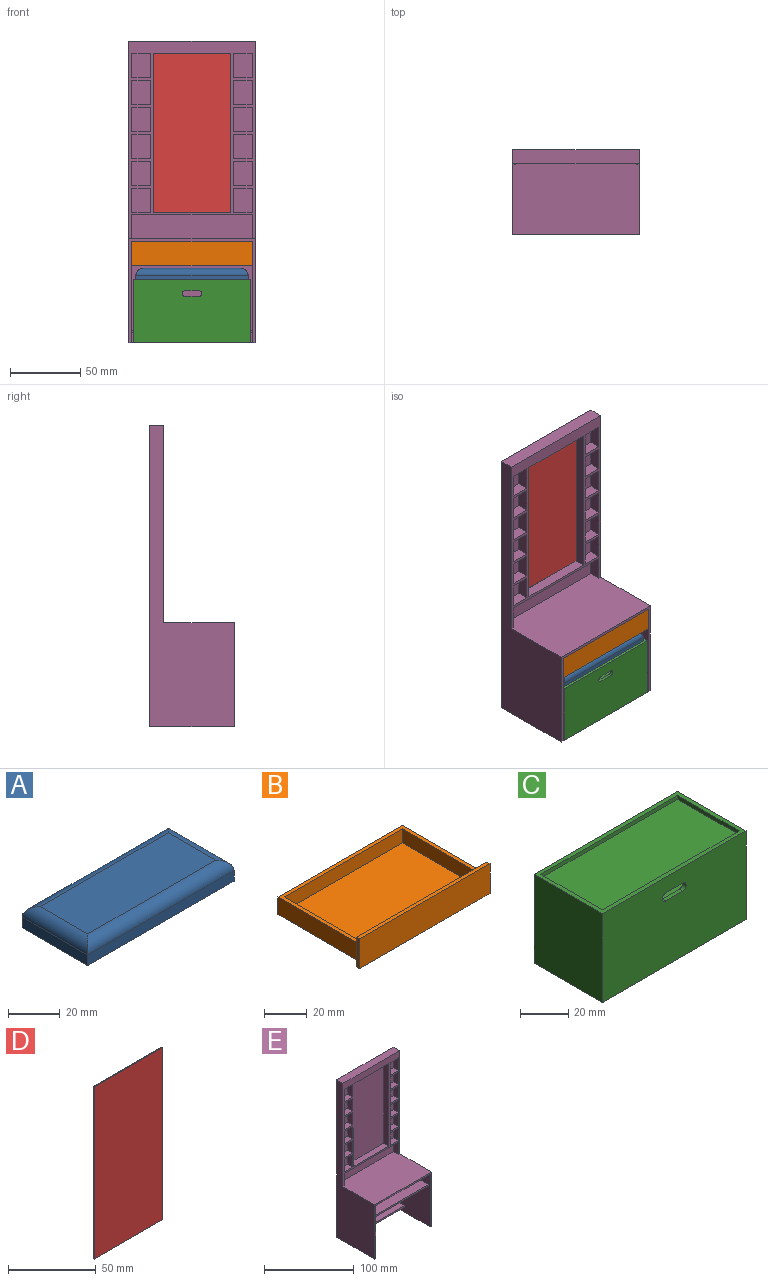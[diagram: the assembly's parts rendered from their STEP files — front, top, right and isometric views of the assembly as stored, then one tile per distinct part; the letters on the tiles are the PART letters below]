
ASSEMBLY  parts=5 mates=4
PART A: 10 faces, bbox 80x36x10 mm
  f0: plane 36x5mm, normal (1,0,0), area 180mm2, adj f1,f3,f5,f6
  f1: plane 80x5mm, normal (0,1,0), area 400mm2, adj f0,f2,f5,f7
  f2: plane 36x5mm, normal (-1,0,0), area 180mm2, adj f1,f3,f5,f9
  f3: plane 80x5mm, normal (0,-1,0), area 400mm2, adj f0,f2,f5,f8
  f4: plane 70x26mm, normal (0,0,1), area 1820mm2, adj f6,f7,f8,f9
  f5: plane 80x36mm, normal (0,0,-1), area 2880mm2, adj f0,f1,f2,f3
  f6: cylinder r=5mm len=36mm, axis (0,-1,0), area 254.2mm2, adj f0,f4,f7,f8
  f7: cylinder r=5mm len=80mm, axis (1,0,0), area 599.8mm2, adj f1,f4,f6,f9
  f8: cylinder r=5mm len=80mm, axis (-1,0,0), area 599.8mm2, adj f3,f4,f6,f9
  f9: cylinder r=5mm len=36mm, axis (0,1,0), area 254.2mm2, adj f2,f4,f7,f8
PART B: 15 faces, bbox 86x56x17 mm
  f0: plane 17x2mm, normal (1,0,0), area 34mm2, adj f5,f6,f7,f8
  f1: plane 82x10mm, normal (0,1,0), area 820mm2, adj f3,f4,f13,f14
  f2: plane 17x2mm, normal (-1,0,0), area 34mm2, adj f5,f6,f7,f8
  f3: plane 82x54mm, normal (0,0,-1), area 4428mm2, adj f1,f8,f13,f14
  f4: plane 82x54mm, normal (0,0,1), area 372mm2, adj f1,f8,f9,f10,f11,f13,f14
  f5: plane 86x2mm, normal (0,0,-1), area 172mm2, adj f0,f2,f7,f8
  f6: plane 86x2mm, normal (0,0,1), area 172mm2, adj f0,f2,f7,f8
  f7: plane 86x17mm, normal (0,-1,0), area 1462mm2, adj f0,f2,f5,f6
  f8: plane 86x17mm, normal (0,1,0), area 1266mm2, adj f0,f2,f3,f4,f5,f6,f10,f11
  f9: plane 78x8mm, normal (0,-1,0), area 624mm2, adj f4,f10,f11,f12
  f10: plane 52x8mm, normal (1,0,0), area 416mm2, adj f4,f8,f9,f12
  f11: plane 52x8mm, normal (-1,0,0), area 416mm2, adj f4,f8,f9,f12
  f12: plane 78x52mm, normal (0,0,1), area 4056mm2, adj f8,f9,f10,f11
  f13: plane 54x10mm, normal (-1,0,0), area 540mm2, adj f1,f3,f4,f8
  f14: plane 54x10mm, normal (1,0,0), area 540mm2, adj f1,f3,f4,f8
PART C: 25 faces, bbox 84x40x45 mm
  f0: plane 84x45mm, normal (0,1,0), area 820mm2, adj f1,f2,f3,f4,f6,f7,f8,f9
  f1: plane 45x40mm, normal (-1,0,0), area 1800mm2, adj f0,f2,f4,f5
  f2: plane 84x40mm, normal (0,0,-1), area 3360mm2, adj f0,f1,f3,f5
  f3: plane 45x40mm, normal (1,0,0), area 1800mm2, adj f0,f2,f4,f5
  f4: plane 84x40mm, normal (0,0,1), area 480mm2, adj f0,f1,f3,f5,f16,f17,f18,f19
  f5: plane 84x45mm, normal (0,-1,0), area 3727.4mm2, adj f1,f2,f3,f4,f21,f22,f23,f24
  f6: plane 38x18.5mm, normal (-1,0,0), area 703mm2, adj f0,f7,f9,f10
  f7: plane 80x38mm, normal (0,0,1), area 3040mm2, adj f0,f6,f8,f10
  f8: plane 38x18.5mm, normal (1,0,0), area 703mm2, adj f0,f7,f9,f10
  f9: plane 80x38mm, normal (0,0,-1), area 3040mm2, adj f0,f6,f8,f10
  f10: plane 80x18.5mm, normal (0,1,0), area 1427.4mm2, adj f6,f7,f8,f9,f21,f22,f23,f24
  f11: plane 38x18.5mm, normal (-1,0,0), area 703mm2, adj f0,f12,f14,f15
  f12: plane 80x38mm, normal (0,0,1), area 3040mm2, adj f0,f11,f13,f15
  f13: plane 38x18.5mm, normal (1,0,0), area 703mm2, adj f0,f12,f14,f15
  f14: plane 80x38mm, normal (0,0,-1), area 3040mm2, adj f0,f11,f13,f15
  f15: plane 80x18.5mm, normal (0,1,0), area 1480mm2, adj f11,f12,f13,f14
  f16: plane 80x2mm, normal (0,-1,0), area 160mm2, adj f4,f17,f19,f20
  f17: plane 36x2mm, normal (1,0,0), area 72mm2, adj f4,f16,f18,f20
  f18: plane 80x2mm, normal (0,1,0), area 160mm2, adj f4,f17,f19,f20
  f19: plane 36x2mm, normal (-1,0,0), area 72mm2, adj f4,f16,f18,f20
  f20: plane 80x36mm, normal (0,0,1), area 2880mm2, adj f16,f17,f18,f19
  f21: plane 10x2mm, normal (0,0,-1), area 20mm2, adj f5,f10,f22,f24
  f22: cylinder r=2mm len=4mm, axis (0,-1,0), area 12.6mm2, adj f5,f10,f21,f23
  f23: plane 10x2mm, normal (0,0,1), area 20mm2, adj f5,f10,f22,f24
  f24: cylinder r=2mm len=4mm, axis (0,-1,0), area 12.6mm2, adj f5,f10,f21,f23
PART D: 6 faces, bbox 55x0.5x119.9 mm
  f0: plane 55x0.5mm, normal (0,0,-1), area 27.5mm2, adj f1,f3,f4,f5
  f1: plane 119.86x0.5mm, normal (1,0,0), area 59.9mm2, adj f0,f2,f4,f5
  f2: plane 55x0.5mm, normal (0,0,1), area 27.5mm2, adj f1,f3,f4,f5
  f3: plane 119.86x0.5mm, normal (-1,0,0), area 59.9mm2, adj f0,f2,f4,f5
  f4: plane 119.86x55mm, normal (0,-1,0), area 6592.1mm2, adj f0,f1,f2,f3
  f5: plane 119.86x55mm, normal (0,1,0), area 6592.1mm2, adj f0,f1,f2,f3
PART E: 95 faces, bbox 90x60x215 mm
  f0: plane 86x46mm, normal (0,-1,0), area 3956mm2, adj f1,f12,f16,f93
  f1: plane 72x58mm, normal (1,0,0), area 4028mm2, adj f0,f5,f6,f12,f13,f14,f15,f17
  f2: plane 13.5x2mm, normal (0,0,-1), area 27mm2, adj f4,f48,f50,f89
  f3: plane 55x2mm, normal (0,0,-1), area 110mm2, adj f4,f19,f21,f86
  f4: plane 141x90mm, normal (0,-1,0), area 2231.4mm2, adj f2,f3,f8,f9,f10,f11,f19,f20
  f5: plane 90x60mm, normal (0,0,-1), area 412mm2, adj f1,f6,f7,f10,f11,f13,f16
  f6: plane 90x74mm, normal (0,-1,0), area 468mm2, adj f1,f5,f9,f10,f11,f14,f16
  f7: plane 215x90mm, normal (0,1,0), area 19350mm2, adj f5,f8,f10,f11
  f8: plane 90x10mm, normal (0,0,1), area 900mm2, adj f4,f7,f10,f11
  f9: plane 90x58mm, normal (0,0,1), area 5188mm2, adj f4,f6,f10,f11,f71,f73,f74
  f10: plane 215x60mm, normal (1,0,0), area 5850mm2, adj f4,f5,f6,f7,f8,f9
  f11: plane 215x60mm, normal (-1,0,0), area 5850mm2, adj f4,f5,f6,f7,f8,f9
  f12: plane 86x56mm, normal (0,0,-1), area 4816mm2, adj f0,f1,f16,f85
  f13: plane 86x7mm, normal (0,-1,0), area 602mm2, adj f1,f5,f16,f92
  f14: plane 86x58mm, normal (0,0,-1), area 4988mm2, adj f1,f6,f16,f17
  f15: plane 86x56mm, normal (0,0,1), area 4816mm2, adj f1,f16,f17,f85
  f16: plane 72x58mm, normal (-1,0,0), area 4028mm2, adj f0,f5,f6,f12,f13,f14,f15,f17
  f17: plane 86x15mm, normal (0,-1,0), area 1290mm2, adj f1,f14,f15,f16
  f18: plane 119.86x55mm, normal (0,-1,0), area 6592.1mm2, adj f19,f20,f21,f87
  f19: plane 119.86x8mm, normal (1,0,0), area 944.9mm2, adj f3,f4,f18,f20,f86,f87
  f20: plane 55x8mm, normal (0,0,1), area 440mm2, adj f4,f18,f19,f21
  f21: plane 119.86x8mm, normal (-1,0,0), area 944.9mm2, adj f3,f4,f18,f20,f86,f87
  f22: plane 17.14x13.5mm, normal (0,-1,0), area 231.4mm2, adj f23,f24,f25,f26
  f23: plane 17.14x8mm, normal (1,0,0), area 137.1mm2, adj f4,f22,f24,f25
  f24: plane 13.5x8mm, normal (0,0,-1), area 108mm2, adj f4,f22,f23,f26
  f25: plane 13.5x8mm, normal (0,0,1), area 108mm2, adj f4,f22,f23,f26
  f26: plane 17.14x8mm, normal (-1,0,0), area 137.1mm2, adj f4,f22,f24,f25
  f27: plane 17.14x13.5mm, normal (0,-1,0), area 231.4mm2, adj f28,f29,f30,f31
  f28: plane 17.14x8mm, normal (1,0,0), area 137.1mm2, adj f4,f27,f29,f30
  f29: plane 13.5x8mm, normal (0,0,-1), area 108mm2, adj f4,f27,f28,f31
  f30: plane 13.5x8mm, normal (0,0,1), area 108mm2, adj f4,f27,f28,f31
  f31: plane 17.14x8mm, normal (-1,0,0), area 137.1mm2, adj f4,f27,f29,f30
  f32: plane 17.14x13.5mm, normal (0,-1,0), area 231.4mm2, adj f33,f34,f35,f36
  f33: plane 17.14x8mm, normal (1,0,0), area 137.1mm2, adj f4,f32,f34,f35
  f34: plane 13.5x8mm, normal (0,0,-1), area 108mm2, adj f4,f32,f33,f36
  f35: plane 13.5x8mm, normal (0,0,1), area 108mm2, adj f4,f32,f33,f36
  f36: plane 17.14x8mm, normal (-1,0,0), area 137.1mm2, adj f4,f32,f34,f35
  f37: plane 17.14x13.5mm, normal (0,-1,0), area 231.4mm2, adj f38,f39,f40,f41
  f38: plane 17.14x8mm, normal (1,0,0), area 137.1mm2, adj f4,f37,f39,f40
  f39: plane 13.5x8mm, normal (0,0,-1), area 108mm2, adj f4,f37,f38,f41
  f40: plane 13.5x8mm, normal (0,0,1), area 108mm2, adj f4,f37,f38,f41
  f41: plane 17.14x8mm, normal (-1,0,0), area 137.1mm2, adj f4,f37,f39,f40
  f42: plane 17.14x13.5mm, normal (0,-1,0), area 231.4mm2, adj f43,f44,f45,f46
  f43: plane 17.14x8mm, normal (1,0,0), area 137.1mm2, adj f4,f42,f44,f45
  f44: plane 13.5x8mm, normal (0,0,-1), area 108mm2, adj f4,f42,f43,f46
  f45: plane 13.5x8mm, normal (0,0,1), area 108mm2, adj f4,f42,f43,f46
  f46: plane 17.14x8mm, normal (-1,0,0), area 137.1mm2, adj f4,f42,f44,f45
  f47: plane 24.14x13.5mm, normal (0,-1,0), area 325.9mm2, adj f48,f49,f50,f88
  f48: plane 24.14x8mm, normal (1,0,0), area 179.1mm2, adj f2,f4,f47,f49,f88,f89
  f49: plane 13.5x8mm, normal (0,0,1), area 108mm2, adj f4,f47,f48,f50
  f50: plane 24.14x8mm, normal (-1,0,0), area 179.1mm2, adj f2,f4,f47,f49,f88,f89
  f51: plane 17.14x13.5mm, normal (0,-1,0), area 231.4mm2, adj f52,f53,f54,f55
  f52: plane 17.14x8mm, normal (1,0,0), area 137.1mm2, adj f4,f51,f53,f54
  f53: plane 13.5x8mm, normal (0,0,-1), area 108mm2, adj f4,f51,f52,f55
  f54: plane 13.5x8mm, normal (0,0,1), area 108mm2, adj f4,f51,f52,f55
  f55: plane 17.14x8mm, normal (-1,0,0), area 137.1mm2, adj f4,f51,f53,f54
  f56: plane 17.14x13.5mm, normal (0,-1,0), area 231.4mm2, adj f57,f58,f59,f60
  f57: plane 17.14x8mm, normal (1,0,0), area 137.1mm2, adj f4,f56,f58,f59
  f58: plane 13.5x8mm, normal (0,0,-1), area 108mm2, adj f4,f56,f57,f60
  f59: plane 13.5x8mm, normal (0,0,1), area 108mm2, adj f4,f56,f57,f60
  f60: plane 17.14x8mm, normal (-1,0,0), area 137.1mm2, adj f4,f56,f58,f59
  f61: plane 17.14x13.5mm, normal (0,-1,0), area 231.4mm2, adj f62,f63,f64,f65
  f62: plane 17.14x8mm, normal (1,0,0), area 137.1mm2, adj f4,f61,f63,f64
  f63: plane 13.5x8mm, normal (0,0,-1), area 108mm2, adj f4,f61,f62,f65
  f64: plane 13.5x8mm, normal (0,0,1), area 108mm2, adj f4,f61,f62,f65
  f65: plane 17.14x8mm, normal (-1,0,0), area 137.1mm2, adj f4,f61,f63,f64
  f66: plane 24.14x13.5mm, normal (0,-1,0), area 325.9mm2, adj f67,f68,f69,f90
  f67: plane 13.5x8mm, normal (0,0,1), area 108mm2, adj f4,f66,f68,f69
  f68: plane 24.14x8mm, normal (1,0,0), area 179.1mm2, adj f4,f66,f67,f70,f90,f91
  f69: plane 24.14x8mm, normal (-1,0,0), area 179.1mm2, adj f4,f66,f67,f70,f90,f91
  f70: plane 13.5x2mm, normal (0,0,-1), area 27mm2, adj f4,f68,f69,f91
  f71: plane 86x17.14mm, normal (0,-1,0), area 1474.3mm2, adj f9,f72,f73,f74
  f72: plane 86x8mm, normal (0,0,-1), area 688mm2, adj f4,f71,f73,f74
  f73: plane 17.14x8mm, normal (-1,0,0), area 137.1mm2, adj f4,f9,f71,f72
  f74: plane 17.14x8mm, normal (1,0,0), area 137.1mm2, adj f4,f9,f71,f72
  f75: plane 17.14x13.5mm, normal (0,-1,0), area 231.4mm2, adj f76,f77,f78,f79
  f76: plane 17.14x8mm, normal (1,0,0), area 137.1mm2, adj f4,f75,f77,f78
  f77: plane 13.5x8mm, normal (0,0,-1), area 108mm2, adj f4,f75,f76,f79
  f78: plane 13.5x8mm, normal (0,0,1), area 108mm2, adj f4,f75,f76,f79
  f79: plane 17.14x8mm, normal (-1,0,0), area 137.1mm2, adj f4,f75,f77,f78
  f80: plane 17.14x13.5mm, normal (0,-1,0), area 231.4mm2, adj f81,f82,f83,f84
  f81: plane 17.14x8mm, normal (1,0,0), area 137.1mm2, adj f4,f80,f82,f83
  f82: plane 13.5x8mm, normal (0,0,-1), area 108mm2, adj f4,f80,f81,f84
  f83: plane 13.5x8mm, normal (0,0,1), area 108mm2, adj f4,f80,f81,f84
  f84: plane 17.14x8mm, normal (-1,0,0), area 137.1mm2, adj f4,f80,f82,f83
  f85: plane 86x2mm, normal (0,-1,0), area 172mm2, adj f1,f12,f15,f16
  f86: plane 55x7mm, normal (0,1,0), area 385mm2, adj f3,f19,f21,f87
  f87: plane 55x6mm, normal (0,0,-1), area 330mm2, adj f18,f19,f21,f86
  f88: plane 13.5x6mm, normal (0,0,-1), area 81mm2, adj f47,f48,f50,f89
  f89: plane 13.5x7mm, normal (0,1,0), area 94.5mm2, adj f2,f48,f50,f88
  f90: plane 13.5x6mm, normal (0,0,-1), area 81mm2, adj f66,f68,f69,f91
  f91: plane 13.5x7mm, normal (0,1,0), area 94.5mm2, adj f68,f69,f70,f90
  f92: plane 86x18mm, normal (0,0,-1), area 1548mm2, adj f1,f13,f16,f94
  f93: plane 86x18mm, normal (0,0,1), area 1548mm2, adj f0,f1,f16,f94
  f94: plane 86x2mm, normal (0,-1,0), area 172mm2, adj f1,f16,f92,f93
PLACE A t=(-186.54,216.24,-95.56)mm
PLACE B t=(-186.54,116.24,-5.56)mm
PLACE C t=(-186.54,216.24,-5.56)mm
PLACE D t=(-186.54,115.74,-5.56)mm
PLACE E t=(-186.54,16.24,-5.56)mm fixed
MATE slider B.f7 <-> E.f6  axis (0,-1,0) through (-98.54,-43.76,66.44)mm
MATE fastened A.f5 <-> C.f20  axis (0,0,-1) through (-101.54,-41.76,37.44)mm
MATE slider C.f5 <-> E.f6  axis (0,-1,0) through (-99.54,-43.76,-5.56)mm
MATE fastened D.f5 <-> E.f18  axis (0,1,0) through (-169.04,14.24,87.59)mm
